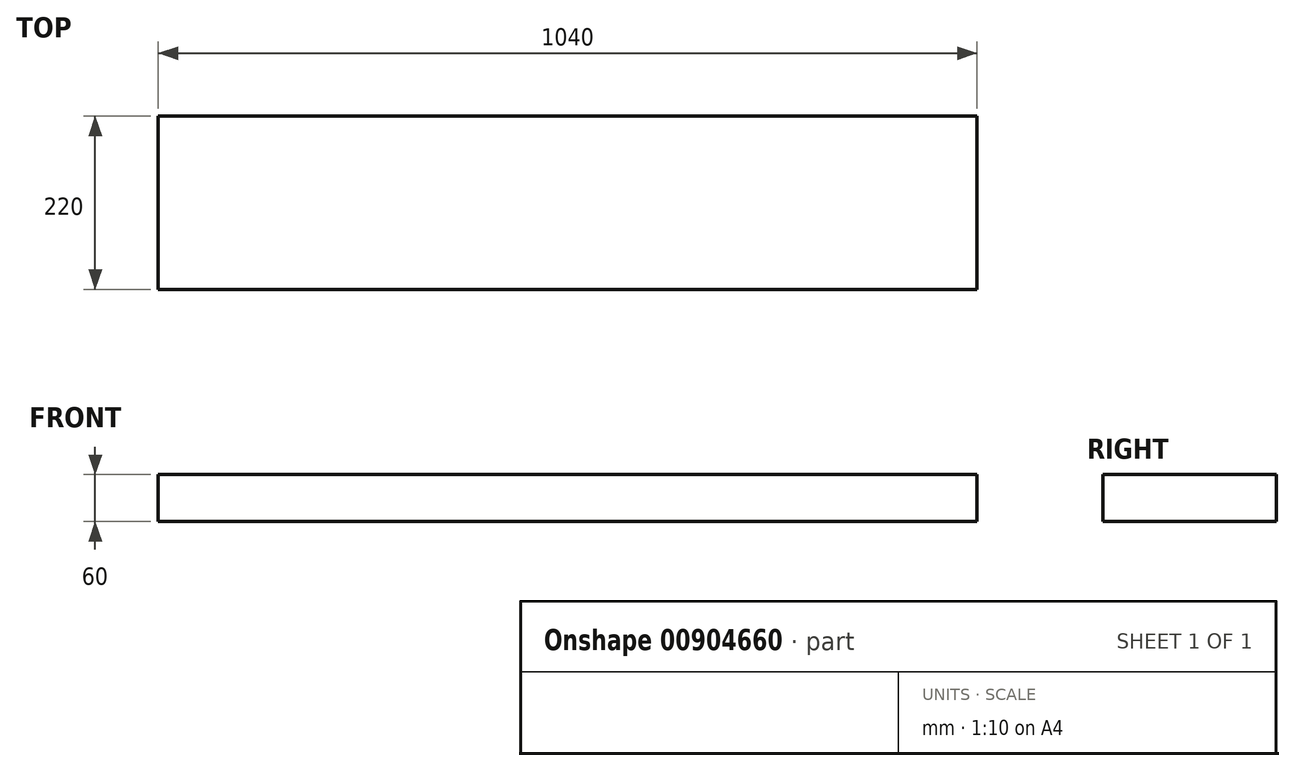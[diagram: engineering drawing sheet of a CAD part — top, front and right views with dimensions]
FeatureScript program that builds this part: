
annotation { "Feature Type Name" : "Feature", "Feature Type Description" : "" }
export const myFeature = defineFeature(function(context is Context, id is Id, definition is map)
    precondition{}
    {
        {
            var Q0;
            Q0=qCreatedBy(makeId("Top.planeOp"),FACE);
            var sketch = newSketch(context, id + "F0", { "sketchPlane" : qUnion([Q0])});
            skLineSegment(sketch, "E0.bottom", {"start": v(0, 0) * mm, "end": v(-1040, 0) * mm});
            skLineSegment(sketch, "E0.top", {"start": v(0, 220) * mm, "end": v(-1040, 220) * mm});
            skLineSegment(sketch, "E0.left", {"start": v(0, 0) * mm, "end": v(0, 220) * mm});
            skLineSegment(sketch, "E0.right", {"start": v(-1040, 0) * mm, "end": v(-1040, 220) * mm});
            skSolve(sketch);
        }
        {
            var Q0;
            Q0=qSketchRegion(id+"F0",true);
            extrude(context, id + "F1", {"entities" : qUnion([Q0]), "depth" : 60 * mm, "offsetDistance" : 25 * mm});
        }
    });
